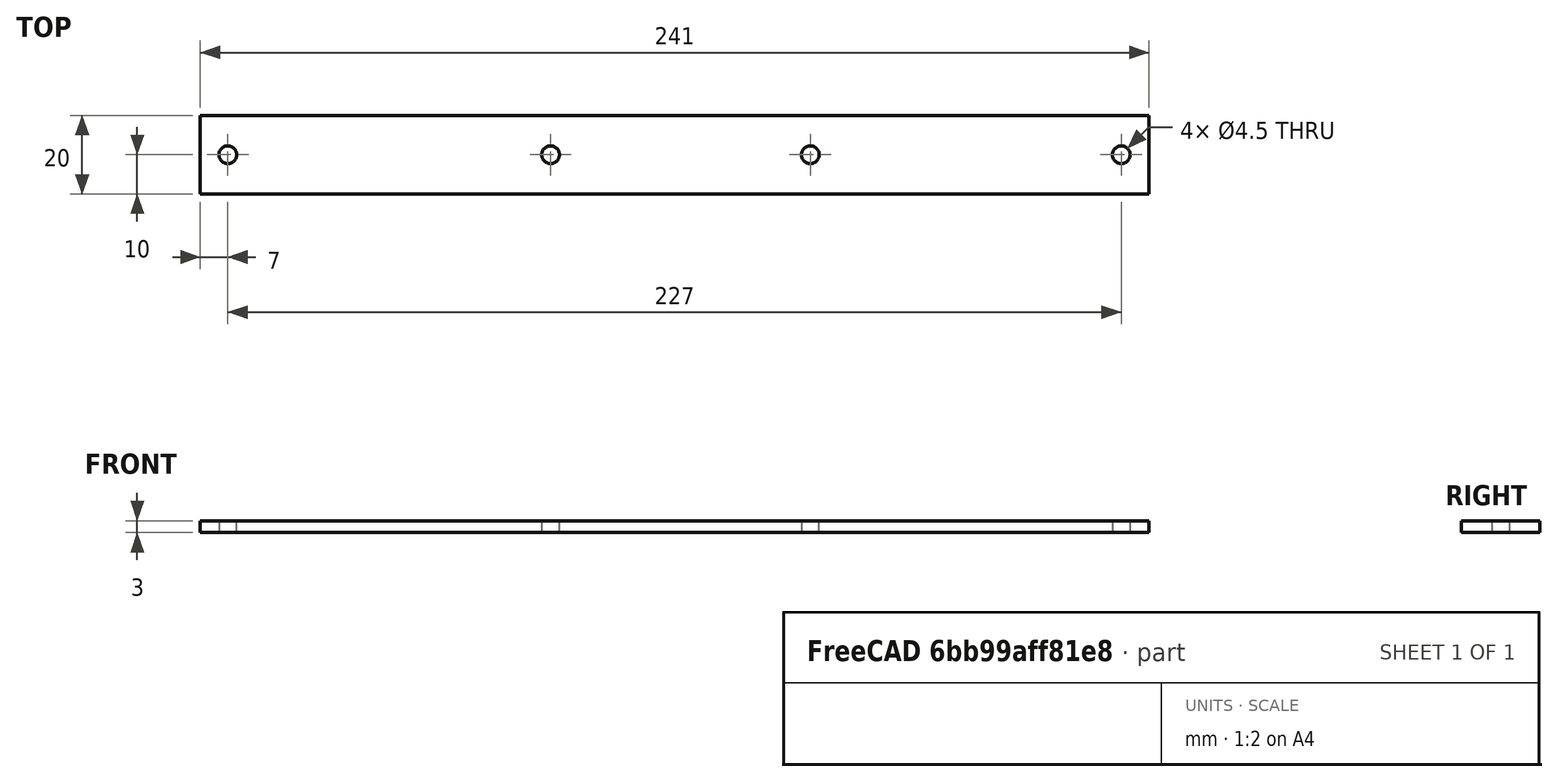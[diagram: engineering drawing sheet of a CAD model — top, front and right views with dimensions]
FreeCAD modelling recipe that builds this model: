
FCSTD DOCUMENT  (FreeCAD 0.21R33668 +26 (Git))
Label: 1-folding-hinge-rear-bar
License: All rights reserved
LicenseURL: http://en.wikipedia.org/wiki/All_rights_reserved
objects: PartDesign::SubtractiveCylinder×4, PartDesign::AdditiveBox×1, PartDesign::Body×1
note: 11 computed .brp shape members not serialized (recipe doc carries the construction recipe); baked Part::Feature solids carry a one-line shape summary decoded from their .brp

FEATURE [PartDesign::AdditiveBox] Box  label="bar"
  AttacherType = Attacher::AttachEngine3D
  Height = 3
  Length = 241
  Width = 20
FEATURE [PartDesign::SubtractiveCylinder] Cylinder  label="mp1"
  Angle = 360
  AttacherType = Attacher::AttachEngine3D
  AttachmentOffset = pos=(7,10,-3) rot=(0,0,1;0rad)
  BaseFeature = -> Box
  FirstAngle = 0
  Height = 3
  MapMode = 5
  Placement = pos=(7,10,0) rot=(0,0,1;0rad)
  Radius = 2.25
  SecondAngle = 0
  Support = -> [Box]
FEATURE [PartDesign::SubtractiveCylinder] Cylinder001  label="mp2"
  Angle = 360
  AttacherType = Attacher::AttachEngine3D
  AttachmentOffset = pos=(227,0,-3) rot=(0,0,1;0rad)
  BaseFeature = -> Cylinder
  FirstAngle = 0
  Height = 3
  MapMode = 5
  Placement = pos=(234,10,0) rot=(0,0,1;0rad)
  Radius = 2.25
  SecondAngle = 0
  Support = -> [Cylinder]
FEATURE [PartDesign::SubtractiveCylinder] Cylinder002  label="hinge-mp1"
  Angle = 360
  AttacherType = Attacher::AttachEngine3D
  AttachmentOffset = pos=(-145,0,-3) rot=(0,0,1;0rad)
  BaseFeature = -> Cylinder001
  FirstAngle = 0
  Height = 3
  MapMode = 5
  Placement = pos=(89,10,0) rot=(0,0,1;0rad)
  Radius = 2.25
  SecondAngle = 0
  Support = -> [Cylinder001]
FEATURE [PartDesign::SubtractiveCylinder] Cylinder003  label="hinge-mp2"
  Angle = 360
  AttacherType = Attacher::AttachEngine3D
  AttachmentOffset = pos=(66,0,-3) rot=(0,0,1;0rad)
  BaseFeature = -> Cylinder002
  FirstAngle = 0
  Height = 3
  MapMode = 5
  Placement = pos=(155,10,0) rot=(0,0,1;0rad)
  Radius = 2.25
  SecondAngle = 0
  Support = -> [Cylinder002]
FEATURE [PartDesign::Body] Body
  Group = -> [Box,Cylinder,Cylinder001,Cylinder002,Cylinder003]
  Origin = -> Origin
  Tip = -> Cylinder003
